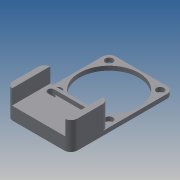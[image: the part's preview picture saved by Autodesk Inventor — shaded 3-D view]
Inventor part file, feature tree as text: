
AUTODESK INVENTOR PART (.ipt)
format: ipt  version: 2013 (Build 170138000, 138)  size: 194,560 bytes
history: native  units: mm
features: extrude x7, sketch x7, fillet x1, projected_geometry x1
ambient origin geometry x8: Origin, YZ Plane, XZ Plane, XY Plane, X Axis, Y Axis, Z Axis, Center Point
bodies: Solid1 (feature_tree)
feature tree (16):
  extrude  "Extrusion1"  Depth=28.0mm
  extrude  "Extrusion2"  Depth=3.5mm
  extrude  "Extrusion3"  Depth=25.0mm
  extrude  "Extrusion4"  Depth=6.0mm TaperAngle=0.0deg
  extrude  "Extrusion5"  Depth=18.25mm
  extrude  "Extrusion6"  Depth=6.0mm TaperAngle=0.0deg
  fillet  "Fillet3"  Radius=2.0mm
  extrude  "Extrusion7"  Depth=7.0mm TaperAngle=0.0deg
  sketch  "Sketch1"  dims[d0=30.4mm d1=28.0mm]
  sketch  "Sketch2"  dims[d2=24.0mm d3=3.5mm]
  sketch  "Sketch3"  dims[d4=6.0mm d5=0.0mm d6=25.0mm]
  sketch  "Sketch4"  dims[d8=18.0mm d9=6.0mm d10=0.0mm]
  sketch  "Sketch5"  dims[d11=3.0mm d12=18.25mm]
  sketch  "Sketch6"  dims[d13=3.1mm d14=6.0mm d15=0.0mm d18=2.0mm d19=0.0mm]
  projected_geometry  "Projected Loop1"
  sketch  "Sketch7"  dims[d20=7.0mm d21=0.0mm d22=7.0mm d23=0.0mm d24=3.2mm d25=4.0mm d26=0.0mm]
